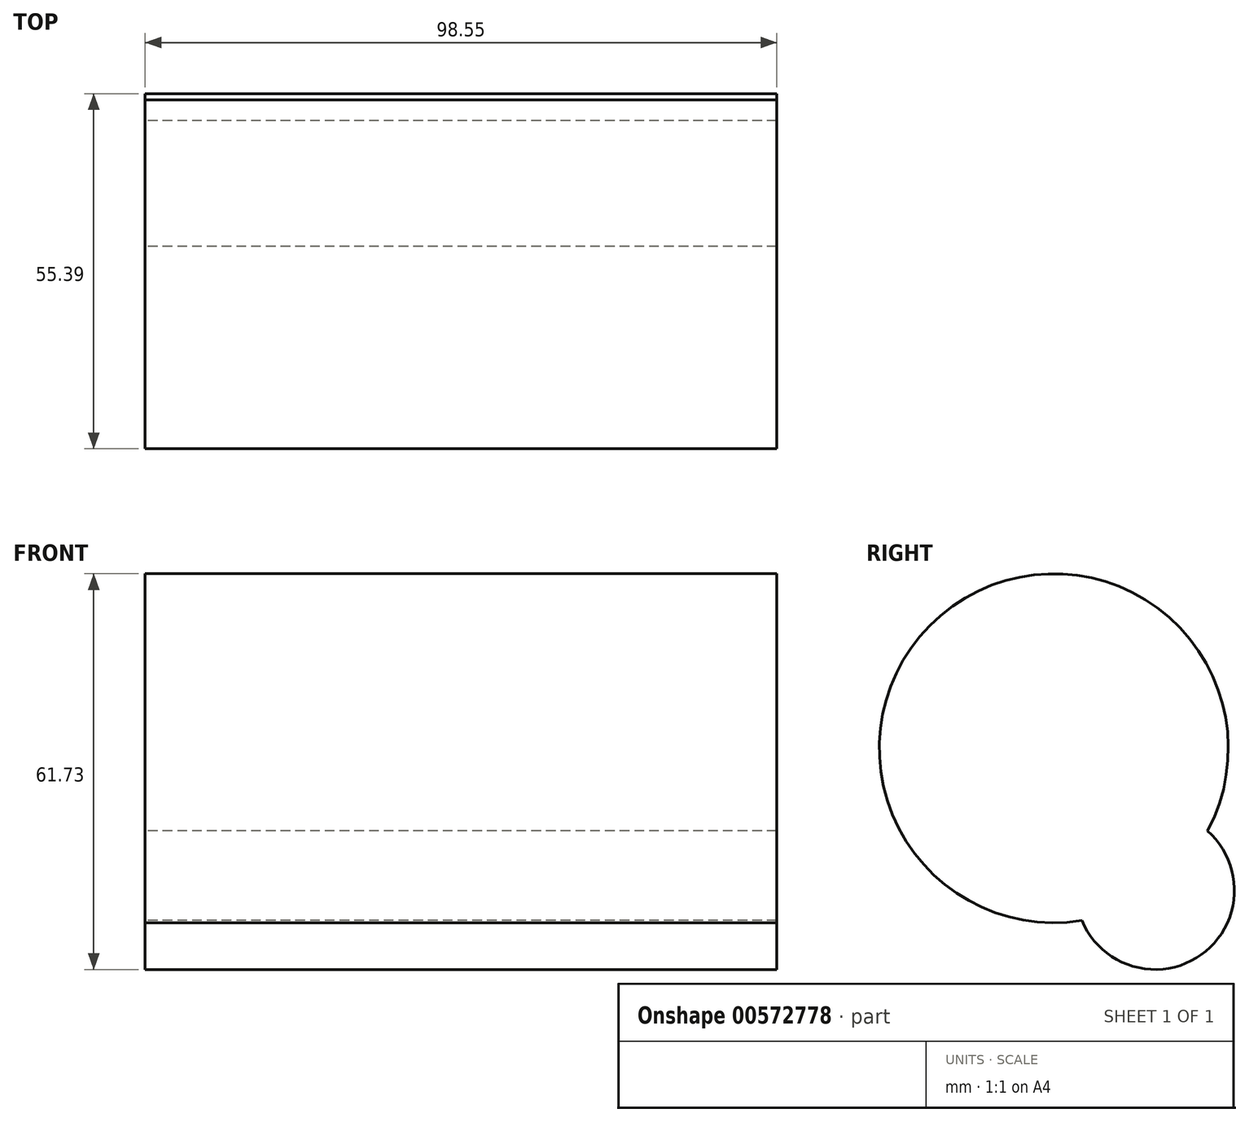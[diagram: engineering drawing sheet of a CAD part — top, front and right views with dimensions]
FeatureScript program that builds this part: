
annotation { "Feature Type Name" : "Feature", "Feature Type Description" : "" }
export const myFeature = defineFeature(function(context is Context, id is Id, definition is map)
    precondition{}
    {
        {
            var Q0;
            Q0=qCreatedBy(makeId("Right.planeOp"),FACE);
            var sketch = newSketch(context, id + "F0", { "sketchPlane" : qUnion([Q0])});
            skCircle(sketch, "E0", {"center": v(5.22, 0) * mm, "radius": 27.22 * mm});
            skCircle(sketch, "E1", {"center": v(21.04, -22.16) * mm, "radius": 12.36 * mm});
            skSolve(sketch);
        }
        {
            var Q0;
            Q0 = qSketchRegion(id + "F0", true);
            extrude(context, id + "F1", {"entities" : qUnion([Q0]), "depth" : 98.55 * mm, "offsetDistance" : 25.4 * mm});
        }
    });
